# Revit family: VIESSMANN - Vitocrossal 300 CRU
name_source: partatom
category: Wyposażenie mechaniczne
revit_build: Autodesk Revit 2017 (Build: 20160720_1515(x64)
units: mm (PartAtom-declared; Revit-internal decimal feet)

## family parameters
Numer OmniClass = 23.15.30.27.21
Oparty na płaszczyźnie roboczej = Nie
Punkt obliczania pomieszczeń = Nie
Tnij formami wycięć po wczytaniu = Tak
Typ części = Normalny
Tytuł OmniClass = Gas Tanks and Gasholders
Współdzielony = Nie
Wymiar okrągłego złącza = Użyj średnicy
Zawsze pionowo = Tak

## types (2) — shared parameters
Autor = https://www.archispace.pl
Ciśnienie kontrolne = 0.8 MPa
Ciśnienie na przyłączu gazu E/GZ50/G20 oraz Lw/GZ41,5/G27 = 1.8 do 2.5 kPa
Częstotliwość = 50 Hz
Dop. maks. ciśnienie robocze = 0.6 MPa
Dop. min. ciśnienie robocze = 0.1 MPa
Dop. temperatura na zasilaniu (=temperatura progowa) = 110 °C
Dop. temperatura robocza = 95 °C
Masa - moduł wymiennika ciepła = 615.00 kg
Masa - palnik = 120.00 kg
Mufa R1/2 do dodatkowych regulatorów = 1 1/4"
Mufa Rp - do ogranicznika ciśnienia = 1 1/4"
NOx = Klasa 6, <56 mg/kWh
Napięcie zasilania = 400 V
Natężenie maks. = 16 A
Numer identyfikacyjny produktu = CE-0085CS0411
Odpływ kondensatu (gwint zewnętrzny) = 1/2"
Opis = Gazowy kocioł grzewczy
Opis indeksowy = CE-0085CS0411
Opory przepływu = 0.0 MPa
PN 6 DN - powrót do kotła = 100 mm  [stored 0.328084 ft]
PN 6 DN - powrót do kotła 2 = 100.00 mm
PN 6 DN - zasilanie z kotła = 100 mm  [stored 0.328084 ft]
Parametry spalin (temperatura spalin Tv/Tr 80/60°C) przy obciążeniu częściowym = 63 °C
Parametry spalin - dyspozycyjne ciśnienie tłoczenia na króćcu spalin = 0.0 MPa
Pobór mocy elektrycznej - przy obciążeniu częściowym = 100 W
Producent = Viessmann Sp.z.o.o.
Przyłącze gazu = 1"
Przyłącze powietrza do spalania z zewnątrz (opcja dodatkowa) = 80 mm  [stored 0.262467 ft]
Przyłącze spalin = 300 mm
Przyłącze zabezpieczające (gwint zewnętrzny) = 2"
Sprawność - Hs przy Tv/Tr 80/60°C, obciążenie pełne (100%) = 88 %
Spust = 1 1/4"
Straty postojowe (powyżej temperatury otoczenia) - 30K = 1
Straty postojowe (powyżej temperatury otoczenia) - 50K = 3
Szerokość = 1060 mm  [stored 3.47769 ft]
Szerokość fundamentu = 1200 mm
Typ palnika = MDI
URL = https://www.viessmann-projektant.pl
Viessmann Kolor 1 = Viessmann Kolor 1
Viessmann Kolor 2 = Viessmann Kolor 2
Viessmann Kolor 3 = Viessmann Kolor 3
Współczynnik mocy = 1
Wykonanie palnika = Wbudowany Modulowany
Wysokość = 1550 mm  [stored 5.0853 ft]
Wysokość fundamentu = 100 mm  [stored 0.328084 ft]

## per-type parameters (varying)
- CRU 1000kW: Długość=3260 mm  [stored 10.6955 ft]; Długość fundamentu=2700 mm  [stored 8.85827 ft]; Długość korpusu=3389 mm  [stored 11.1188 ft]; Liczba biegunów=1; Masa - moduł komory spalania=585.00 kg; Masa całkowita=1492.00 kg; Moc nominalna=1000 kW; Model=Gazowy kocioł kondensacyjny Viessmann Vitocrossal 300 CRU 1000kW / Gas condensing boiler Viessmann Vitocrossal 300 CRU 1000kW; Parametry spalin (temperatura spalin Tv/Tr 50/30°C) przy obciążeniu częściowym=35 °C; Parametry spalin (temperatura spalin Tv/Tr 50/30°C) przy znamionowej mocy cieplnej=45 °C; Parametry spalin (temperatura spalin Tv/Tr 80/60°C) przy znamionowej mocy cieplnej=69 °C; Pobór mocy elektrycznej - przy znamionowej mocy cieplnej=2000 W; Pojemność wodna kotła=1180.0 L; Powierzchnia grzewcza=31.50 m²; Poziom mocy akustycznej wg EN 15036=85 dB(A); Przepływ maksymalny=43.20 m³/h; Sprawność - Hs przy Tv/Tr 50/30°C, obciążenie częściowe (30%)=97 %; Sprawność - Hs przy Tv/Tr 50/30°C, obciążenie pełne (100%)=95 %; Sprawność znormalizowana - Hs przy 40/30°C=98 %; Sprawność znormalizowana - Hs przy 75/60°C=96%; Straty energii dyżurnej qB,70=0.7 %; Strumień masowy spalin przy gazie ziemnym GZ-41,5/G27 - przy obciążeniu częściowym=297 kg/h; Strumień masowy spalin przy gazie ziemnym GZ-41,5/G27 - przy znamionowej mocy cieplnej=1592 kg/h; Strumień masowy spalin przy gazie ziemnym GZ-50/G20 - przy obciążeniu częściowym=291 kg/h; Strumień masowy spalin przy gazie ziemnym GZ-50/G20 - przy znamionowej mocy cieplnej=1562 kg/h; Strumień objętości gazu ziemnego Lw/GZ41,5/G27 przy 15°C - przy obciążeniu częściowym=19.60 m³/h; Strumień objętości gazu ziemnego Lw/GZ41,5/G27 przy 15°C - przy znamionowej mocy cieplnej=117.30 m³/h; Strumień objętościowy gazu ziemnego GZ-50/G20 przy 15°C - przy obciążeniu częściowym=16.80 m³/h; Strumień objętościowy gazu ziemnego GZ-50/G20 przy 15°C - przy znamionowej mocy cieplnej=100.80 m³/h; Zakres znamionowego obciążenia cieplnego Qn=159 do 952 kW; Zakres znamionowej mocy cieplnej przy Tv/Tr 50/30°C=171 do 1000 kW; Zakres znamionowej mocy cieplnej przy Tv/Tr 80/60°C=156 do 938 kW
- CRU 800kW: Długość=3060 mm  [stored 10.0394 ft]; Długość fundamentu=2500 mm  [stored 8.2021 ft]; Długość korpusu=3187 mm  [stored 10.456 ft]; Liczba biegunów=3; Masa - moduł komory spalania=535.00 kg; Masa całkowita=1435.00 kg; Moc nominalna=800 kW; Model=Gazowy kocioł kondensacyjny Viessmann Vitocrossal 300 CRU 800kW / Gas condensing boiler Viessmann Vitocrossal 300 CRU 800kW; Parametry spalin (temperatura spalin Tv/Tr 50/30°C) przy obciążeniu częściowym=34 °C; Parametry spalin (temperatura spalin Tv/Tr 50/30°C) przy znamionowej mocy cieplnej=43 °C; Parametry spalin (temperatura spalin Tv/Tr 80/60°C) przy znamionowej mocy cieplnej=67 °C; Pobór mocy elektrycznej - przy znamionowej mocy cieplnej=1500 W; Pojemność wodna kotła=1150.0 L; Powierzchnia grzewcza=24.20 m²; Poziom mocy akustycznej wg EN 15036=83 dB(A); Przepływ maksymalny=34.56 m³/h; Sprawność - Hs przy Tv/Tr 50/30°C, obciążenie częściowe (30%)=98 %; Sprawność - Hs przy Tv/Tr 50/30°C, obciążenie pełne (100%)=96 %; Sprawność znormalizowana - Hs przy 40/30°C=99 %; Sprawność znormalizowana - Hs przy 75/60°C=96 %; Straty energii dyżurnej qB,70=0.4 %; Strumień masowy spalin przy gazie ziemnym GZ-41,5/G27 - przy obciążeniu częściowym=237 kg/h; Strumień masowy spalin przy gazie ziemnym GZ-41,5/G27 - przy znamionowej mocy cieplnej=1273 kg/h; Strumień masowy spalin przy gazie ziemnym GZ-50/G20 - przy obciążeniu częściowym=233 kg/h; Strumień masowy spalin przy gazie ziemnym GZ-50/G20 - przy znamionowej mocy cieplnej=1249 kg/h; Strumień objętości gazu ziemnego Lw/GZ41,5/G27 przy 15°C - przy obciążeniu częściowym=15.60 m³/h; Strumień objętości gazu ziemnego Lw/GZ41,5/G27 przy 15°C - przy znamionowej mocy cieplnej=93.80 m³/h; Strumień objętościowy gazu ziemnego GZ-50/G20 przy 15°C - przy obciążeniu częściowym=13.40 m³/h; Strumień objętościowy gazu ziemnego GZ-50/G20 przy 15°C - przy znamionowej mocy cieplnej=80.60 m³/h; Zakres znamionowego obciążenia cieplnego Qn=127 do 762 kW; Zakres znamionowej mocy cieplnej przy Tv/Tr 50/30°C=137 do 800 kW; Zakres znamionowej mocy cieplnej przy Tv/Tr 80/60°C=125 do 750 kW

note: source unit labels omitted for Straty postojowe (powyżej temperatury otoczenia) - 30K, Straty postojowe (powyżej temperatury otoczenia) - 50K — the stored unit's dimension contradicts the parameter name (converter mislabeling)

note: [stored X ft] marks values corroborated as IEEE doubles in the binary element streams (Revit-internal decimal feet)
